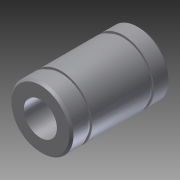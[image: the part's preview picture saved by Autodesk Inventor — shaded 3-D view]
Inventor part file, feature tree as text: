
AUTODESK INVENTOR PART (.ipt)
format: ipt  version: 2012 (Build 160160000, 160)  size: 121,344 bytes
history: native  units: mm
features: revolve x1, sketch x1
ambient origin geometry x8: Origin, YZ Plane, XZ Plane, XY Plane, X Axis, Y Axis, Z Axis, Center Point
bodies: Solid1 (feature_tree)
feature tree (2):
  revolve  "Revolution1"  [1 undecoded]
  sketch  "Sketch1"  dims[d1=1.0mm d2=1.0mm d3=0.5mm d4=0.5mm d5=0.5mm d6=0.5mm d7=24.0mm d8=8.0mm d9=15.0mm d10=4.0mm d11=4.0mm d12=0.5mm d13=90.0deg]
note: 1 required parameter value undecoded (feature->parameter linkage not recoverable at this tier; creation-order binding heuristic only, values carry confidence <= 0.55)
